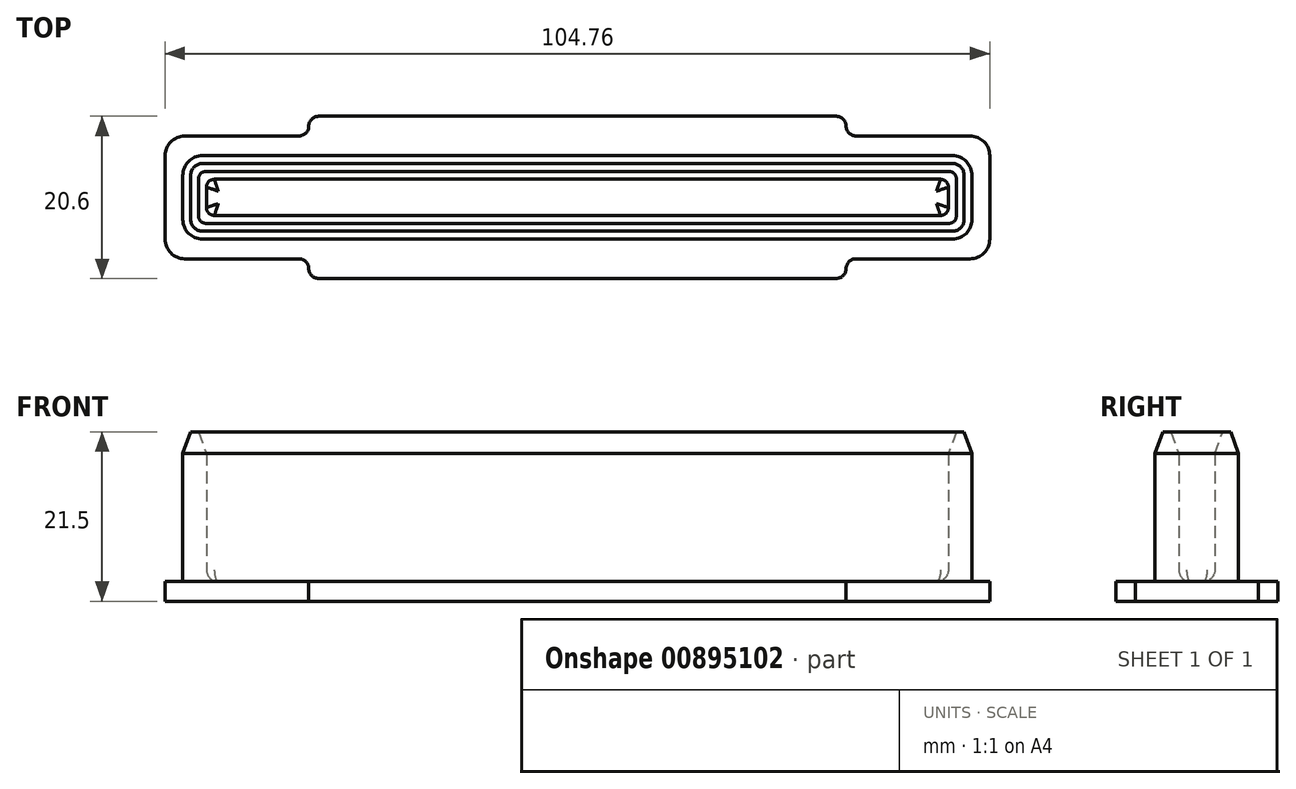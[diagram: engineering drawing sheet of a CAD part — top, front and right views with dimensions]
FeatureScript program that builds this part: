
annotation { "Feature Type Name" : "Feature", "Feature Type Description" : "" }
export const myFeature = defineFeature(function(context is Context, id is Id, definition is map)
    precondition{}
    {
        {
            var Q0;
            Q0=qCreatedBy(makeId("Top.planeOp"),FACE);
            var sketch = newSketch(context, id + "F0", { "sketchPlane" : qUnion([Q0])});
            skLineSegment(sketch, "E0.bottom", {"start": v(50.12, 5.3) * mm, "end": v(-50.12, 5.3) * mm});
            skLineSegment(sketch, "E0.top", {"start": v(50.12, -5.3) * mm, "end": v(-50.12, -5.3) * mm});
            skLineSegment(sketch, "E0.left", {"start": v(50.12, 5.3) * mm, "end": v(50.12, -5.3) * mm});
            skLineSegment(sketch, "E0.right", {"start": v(-50.12, 5.3) * mm, "end": v(-50.12, -5.3) * mm});
            skPoint(sketch, "E0.middle", {"position": v(0, 0) * mm});
            skLineSegment(sketch, "E1.bottom", {"start": v(52.38, 7.8) * mm, "end": v(-52.38, 7.8) * mm});
            skLineSegment(sketch, "E1.top", {"start": v(52.38, -7.8) * mm, "end": v(-52.38, -7.8) * mm});
            skLineSegment(sketch, "E1.left", {"start": v(52.38, 7.8) * mm, "end": v(52.38, -7.8) * mm});
            skLineSegment(sketch, "E1.right", {"start": v(-52.38, 7.8) * mm, "end": v(-52.38, -7.8) * mm});
            skLineSegment(sketch, "E2", {"start": v(0, -22.04) * mm, "end": v(0, 22.45) * mm, "construction": true});
            skLineSegment(sketch, "E3", {"start": v(0, 10.3) * mm, "end": v(34.12, 10.3) * mm});
            skLineSegment(sketch, "E4", {"start": v(34.12, 10.3) * mm, "end": v(34.12, 7.8) * mm});
            skLineSegment(sketch, "E5.MirrorCS", {"start": v(0, 10.3) * mm, "end": v(-34.12, 10.3) * mm});
            skLineSegment(sketch, "E6.MirrorCS", {"start": v(-34.12, 10.3) * mm, "end": v(-34.12, 7.8) * mm});
            skLineSegment(sketch, "E7.MirrorCS", {"start": v(-34.12, -10.3) * mm, "end": v(-34.12, -7.8) * mm});
            skLineSegment(sketch, "E8.MirrorCS", {"start": v(0, -10.3) * mm, "end": v(-34.12, -10.3) * mm});
            skLineSegment(sketch, "E9.MirrorCS", {"start": v(34.13, -10.3) * mm, "end": v(34.13, -7.8) * mm});
            skLineSegment(sketch, "E10.MirrorCS", {"start": v(0, -10.3) * mm, "end": v(34.12, -10.3) * mm});
            skSolve(sketch);
        }
        {
            var Q0;
            Q0=makeQuery(id+"F0.imprint","IMPRINT",FACE,{"disambiguationData":[TD([[makeQuery(id+"F0.imprint","IMPRINT",EDGE,{"derivedFrom":sQuery(id+"F0.wireOp",EDGE,"E0.bottom")}),1.0]])]});
            extrude(context, id + "F1", {"entities" : qUnion([Q0]), "depth" : 19 * mm, "offsetDistance" : 25 * mm});
        }
        {
            var Q0;
            Q0=makeQuery(id+"F1.opExtrude","CAP_FACE",FACE,{"disambiguationData":[OSD([sQuery(id+"F0.wireOp",EDGE,"E0.bottom"),sQuery(id+"F0.wireOp",EDGE,"E0.top"),sQuery(id+"F0.wireOp",EDGE,"E0.left"),sQuery(id+"F0.wireOp",EDGE,"E0.right")])],"isStart":false});
            shell(context, id + "F2", {"entities" : qUnion([Q0]), "thickness" : 3 * mm});
        }
        {
            var Q0;
            Q0=makeQuery(id+"F2.opShell","OFFSET_FACE",FACE,{"disambiguationData":[OSD([sQuery(id+"F0.wireOp",EDGE,"E0.bottom"),sQuery(id+"F0.wireOp",EDGE,"E0.top"),sQuery(id+"F0.wireOp",EDGE,"E0.left"),sQuery(id+"F0.wireOp",EDGE,"E0.right")])]});
            extrude(context, id + "F3", {"entities" : qUnion([Q0]), "operationType" : NewBodyOperationType.REMOVE, "oppositeDirection" : true, "depth" : 25 * mm, "offsetDistance" : 25 * mm});
        }
        {
            var Q0;
            Q0=makeQuery(id+"F0.imprint","IMPRINT",FACE,{"disambiguationData":[TD([[makeQuery(id+"F0.imprint","IMPRINT",EDGE,{"derivedFrom":sQuery(id+"F0.wireOp",EDGE,"E3")}),-1.0]])]});
            var Q1;
            Q1=makeQuery(id+"F0.imprint","IMPRINT",FACE,{"disambiguationData":[TD([[makeQuery(id+"F0.imprint","IMPRINT",EDGE,{"derivedFrom":sQuery(id+"F0.wireOp",EDGE,"E0.bottom")}),-1.0]])]});
            var Q2;
            {var subQ0=sQuery(id+"F0.wireOp",EDGE,"E7.MirrorCS");Q2=makeQuery(id+"F0.imprint","IMPRINT",FACE,{"disambiguationData":[TD([[makeQuery(id+"F0.imprint","IMPRINT",EDGE,{"derivedFrom":subQ0}),-1.0]])]});}
            var Q3;
            Q3=makeQuery(id+"F0.imprint","IMPRINT",FACE,{"disambiguationData":[TD([[makeQuery(id+"F0.imprint","IMPRINT",EDGE,{"derivedFrom":sQuery(id+"F0.wireOp",EDGE,"E0.bottom")}),1.0]])]});
            extrude(context, id + "F4", {"entities" : qUnion([Q0, Q1, Q2, Q3]), "operationType" : NewBodyOperationType.ADD, "oppositeDirection" : true, "depth" : 2.5 * mm, "offsetDistance" : 25 * mm});
        }
        {
            var Q0;
            Q0=makeQuery(id+"F4.opExtrude","SWEPT_EDGE",EDGE,{"disambiguationData":[OSD([sQuery(id+"F0.wireOp",EDGE,"E1.top"),sQuery(id+"F0.wireOp",EDGE,"E1.right")])]});
            var Q1;
            Q1=makeQuery(id+"F4.opExtrude","SWEPT_EDGE",EDGE,{"disambiguationData":[OSD([sQuery(id+"F0.wireOp",EDGE,"E1.bottom"),sQuery(id+"F0.wireOp",EDGE,"E1.right")])]});
            var Q2;
            Q2=makeQuery(id+"F4.opExtrude","SWEPT_EDGE",EDGE,{"disambiguationData":[OSD([sQuery(id+"F0.wireOp",EDGE,"E1.bottom"),sQuery(id+"F0.wireOp",EDGE,"E1.left")])]});
            var Q3;
            Q3=makeQuery(id+"F1.opExtrude","SWEPT_EDGE",EDGE,{"disambiguationData":[OSD([sQuery(id+"F0.wireOp",EDGE,"E0.bottom"),sQuery(id+"F0.wireOp",EDGE,"E0.left")])]});
            var Q4;
            Q4=makeQuery(id+"F1.opExtrude","SWEPT_EDGE",EDGE,{"disambiguationData":[OSD([sQuery(id+"F0.wireOp",EDGE,"E0.top"),sQuery(id+"F0.wireOp",EDGE,"E0.left")])]});
            var Q5;
            Q5=makeQuery(id+"F1.opExtrude","SWEPT_EDGE",EDGE,{"disambiguationData":[OSD([sQuery(id+"F0.wireOp",EDGE,"E0.top"),sQuery(id+"F0.wireOp",EDGE,"E0.right")])]});
            var Q6;
            Q6=makeQuery(id+"F1.opExtrude","SWEPT_EDGE",EDGE,{"disambiguationData":[OSD([sQuery(id+"F0.wireOp",EDGE,"E0.bottom"),sQuery(id+"F0.wireOp",EDGE,"E0.right")])]});
            var Q7;
            Q7=makeQuery(id+"F4.opExtrude","SWEPT_EDGE",EDGE,{"disambiguationData":[OSD([sQuery(id+"F0.wireOp",EDGE,"E1.top"),sQuery(id+"F0.wireOp",EDGE,"E1.left")])]});
            fillet(context, id + "F5", {"entities" : qUnion([Q0, Q1, Q2, Q3, Q4, Q5, Q6, Q7]), "radius" : 2.5 * mm, "tangentPropagation" : true, "allowEdgeOverflow" : false});
        }
        {
            var Q0;
            {var subQ0=sQuery(id+"F0.wireOp",EDGE,"E0.top");Q0=makeQuery(id+"F2.opShell","OFFSET_EDGE",EDGE,{"disambiguationData":[OSD([subQ0]),TDD([makeQuery(id+"F1.opExtrude","CAP_EDGE",EDGE,{"disambiguationData":[OSD([subQ0])],"isStart":false})])]});}
            var Q1;
            Q1=makeQuery(id+"F1.opExtrude","CAP_EDGE",EDGE,{"disambiguationData":[OSD([sQuery(id+"F0.wireOp",EDGE,"E0.top")])],"isStart":false});
            var Q2;
            Q2=makeQuery(id+"F1.opExtrude","CAP_EDGE",EDGE,{"disambiguationData":[OSD([sQuery(id+"F0.wireOp",EDGE,"E0.right")])],"isStart":false});
            var Q3;
            Q3=makeQuery(id+"F1.opExtrude","CAP_EDGE",EDGE,{"disambiguationData":[OSD([sQuery(id+"F0.wireOp",EDGE,"E0.bottom")])],"isStart":false});
            var Q4;
            Q4=makeQuery(id+"F1.opExtrude","CAP_EDGE",EDGE,{"disambiguationData":[OSD([sQuery(id+"F0.wireOp",EDGE,"E0.left")])],"isStart":false});
            var Q5;
            {var subQ0=sQuery(id+"F0.wireOp",EDGE,"E0.left");Q5=makeQuery(id+"F2.opShell","OFFSET_EDGE",EDGE,{"disambiguationData":[OSD([subQ0]),TDD([makeQuery(id+"F1.opExtrude","CAP_EDGE",EDGE,{"disambiguationData":[OSD([subQ0])],"isStart":false})])]});}
            var Q6;
            {var subQ0=sQuery(id+"F0.wireOp",EDGE,"E0.bottom");Q6=makeQuery(id+"F2.opShell","OFFSET_EDGE",EDGE,{"disambiguationData":[OSD([subQ0]),TDD([makeQuery(id+"F1.opExtrude","CAP_EDGE",EDGE,{"disambiguationData":[OSD([subQ0])],"isStart":false})])]});}
            var Q7;
            {var subQ0=sQuery(id+"F0.wireOp",EDGE,"E0.right");Q7=makeQuery(id+"F2.opShell","OFFSET_EDGE",EDGE,{"disambiguationData":[OSD([subQ0]),TDD([makeQuery(id+"F1.opExtrude","CAP_EDGE",EDGE,{"disambiguationData":[OSD([subQ0])],"isStart":false})])]});}
            chamfer(context, id + "F6", {"entities" : qUnion([Q0, Q1, Q2, Q3, Q4, Q5, Q6, Q7]), "chamferType" : ChamferType.OFFSET_ANGLE, "width" : 1 * mm, "oppositeDirection" : false, "angle" : 70 * degree, "tangentPropagation" : true});
        }
        {
            var Q0;
            Q0=makeQuery(id+"F1.opExtrude","CAP_EDGE",EDGE,{"disambiguationData":[OSD([sQuery(id+"F0.wireOp",EDGE,"E0.bottom")])],"isStart":true});
            var Q1;
            Q1=makeQuery(id+"F1.opExtrude","CAP_EDGE",EDGE,{"disambiguationData":[OSD([sQuery(id+"F0.wireOp",EDGE,"E0.left")])],"isStart":true});
            var Q2;
            Q2=makeQuery(id+"F1.opExtrude","CAP_EDGE",EDGE,{"disambiguationData":[OSD([sQuery(id+"F0.wireOp",EDGE,"E0.top")])],"isStart":true});
            var Q3;
            Q3=makeQuery(id+"F1.opExtrude","CAP_EDGE",EDGE,{"disambiguationData":[OSD([sQuery(id+"F0.wireOp",EDGE,"E0.right")])],"isStart":true});
            var Q4;
            {var subQ0=sQuery(id+"F0.wireOp",EDGE,"E0.right");var subQ1=sQuery(id+"F0.wireOp",EDGE,"E0.bottom");Q4=makeQuery(id+"F3.boolean.opBoolean","MERGE",EDGE,{"derivedFrom":[makeQuery(id+"F2.opShell","OFFSET_EDGE",EDGE,{"disambiguationData":[OSD([subQ1,subQ0])]})],"fromTools":[makeQuery(id+"F3.opExtrude","SWEPT_EDGE",EDGE,{"disambiguationData":[OSD([subQ1,subQ0])]})]});}
            var Q5;
            {var subQ0=sQuery(id+"F0.wireOp",EDGE,"E0.left");var subQ1=sQuery(id+"F0.wireOp",EDGE,"E0.bottom");Q5=makeQuery(id+"F3.boolean.opBoolean","MERGE",EDGE,{"derivedFrom":[makeQuery(id+"F2.opShell","OFFSET_EDGE",EDGE,{"disambiguationData":[OSD([subQ1,subQ0])]})],"fromTools":[makeQuery(id+"F3.opExtrude","SWEPT_EDGE",EDGE,{"disambiguationData":[OSD([subQ1,subQ0])]})]});}
            var Q6;
            {var subQ0=sQuery(id+"F0.wireOp",EDGE,"E0.right");var subQ1=sQuery(id+"F0.wireOp",EDGE,"E0.top");Q6=makeQuery(id+"F3.boolean.opBoolean","MERGE",EDGE,{"derivedFrom":[makeQuery(id+"F2.opShell","OFFSET_EDGE",EDGE,{"disambiguationData":[OSD([subQ1,subQ0])]})],"fromTools":[makeQuery(id+"F3.opExtrude","SWEPT_EDGE",EDGE,{"disambiguationData":[OSD([subQ1,subQ0])]})]});}
            var Q7;
            {var subQ0=sQuery(id+"F0.wireOp",EDGE,"E0.left");var subQ1=sQuery(id+"F0.wireOp",EDGE,"E0.top");Q7=makeQuery(id+"F3.boolean.opBoolean","MERGE",EDGE,{"derivedFrom":[makeQuery(id+"F2.opShell","OFFSET_EDGE",EDGE,{"disambiguationData":[OSD([subQ1,subQ0])]})],"fromTools":[makeQuery(id+"F3.opExtrude","SWEPT_EDGE",EDGE,{"disambiguationData":[OSD([subQ1,subQ0])]})]});}
            var Q8;
            {var subQ0=sQuery(id+"F0.wireOp",EDGE,"E0.right");var subQ1=sQuery(id+"F0.wireOp",EDGE,"E0.bottom");Q8=makeQuery(id+"F6.opChamfer","BLEND_EDGE",EDGE,{"blendedFrom":[makeQuery(id+"F2.opShell","OFFSET_EDGE",EDGE,{"disambiguationData":[OSD([subQ1]),TDD([makeQuery(id+"F1.opExtrude","CAP_EDGE",EDGE,{"disambiguationData":[OSD([subQ1])],"isStart":false})])]}),makeQuery(id+"F2.opShell","OFFSET_EDGE",EDGE,{"disambiguationData":[OSD([subQ0]),TDD([makeQuery(id+"F1.opExtrude","CAP_EDGE",EDGE,{"disambiguationData":[OSD([subQ0])],"isStart":false})])]})],"blendedInto":[]});}
            var Q9;
            {var subQ0=sQuery(id+"F0.wireOp",EDGE,"E0.left");var subQ1=sQuery(id+"F0.wireOp",EDGE,"E0.bottom");Q9=makeQuery(id+"F6.opChamfer","BLEND_EDGE",EDGE,{"blendedFrom":[makeQuery(id+"F2.opShell","OFFSET_EDGE",EDGE,{"disambiguationData":[OSD([subQ1]),TDD([makeQuery(id+"F1.opExtrude","CAP_EDGE",EDGE,{"disambiguationData":[OSD([subQ1])],"isStart":false})])]}),makeQuery(id+"F2.opShell","OFFSET_EDGE",EDGE,{"disambiguationData":[OSD([subQ0]),TDD([makeQuery(id+"F1.opExtrude","CAP_EDGE",EDGE,{"disambiguationData":[OSD([subQ0])],"isStart":false})])]})],"blendedInto":[]});}
            var Q10;
            {var subQ0=sQuery(id+"F0.wireOp",EDGE,"E0.right");var subQ1=sQuery(id+"F0.wireOp",EDGE,"E0.top");Q10=makeQuery(id+"F6.opChamfer","BLEND_EDGE",EDGE,{"blendedFrom":[makeQuery(id+"F2.opShell","OFFSET_EDGE",EDGE,{"disambiguationData":[OSD([subQ1]),TDD([makeQuery(id+"F1.opExtrude","CAP_EDGE",EDGE,{"disambiguationData":[OSD([subQ1])],"isStart":false})])]}),makeQuery(id+"F2.opShell","OFFSET_EDGE",EDGE,{"disambiguationData":[OSD([subQ0]),TDD([makeQuery(id+"F1.opExtrude","CAP_EDGE",EDGE,{"disambiguationData":[OSD([subQ0])],"isStart":false})])]})],"blendedInto":[]});}
            var Q11;
            {var subQ0=sQuery(id+"F0.wireOp",EDGE,"E0.left");var subQ1=sQuery(id+"F0.wireOp",EDGE,"E0.top");Q11=makeQuery(id+"F6.opChamfer","BLEND_EDGE",EDGE,{"blendedFrom":[makeQuery(id+"F2.opShell","OFFSET_EDGE",EDGE,{"disambiguationData":[OSD([subQ1]),TDD([makeQuery(id+"F1.opExtrude","CAP_EDGE",EDGE,{"disambiguationData":[OSD([subQ1])],"isStart":false})])]}),makeQuery(id+"F2.opShell","OFFSET_EDGE",EDGE,{"disambiguationData":[OSD([subQ0]),TDD([makeQuery(id+"F1.opExtrude","CAP_EDGE",EDGE,{"disambiguationData":[OSD([subQ0])],"isStart":false})])]})],"blendedInto":[]});}
            fillet(context, id + "F7", {"entities" : qUnion([Q0, Q1, Q2, Q3, Q4, Q5, Q6, Q7, Q8, Q9, Q10, Q11]), "radius" : 1 * mm, "tangentPropagation" : true, "allowEdgeOverflow" : false});
        }
        {
            var Q0;
            Q0=makeQuery(id+"F4.opExtrude","SWEPT_EDGE",EDGE,{"disambiguationData":[OSD([sQuery(id+"F0.wireOp",EDGE,"E5.MirrorCS"),sQuery(id+"F0.wireOp",EDGE,"E6.MirrorCS")])]});
            var Q1;
            Q1=makeQuery(id+"F4.opExtrude","SWEPT_EDGE",EDGE,{"disambiguationData":[OSD([sQuery(id+"F0.wireOp",EDGE,"E3"),sQuery(id+"F0.wireOp",EDGE,"E4")])]});
            var Q2;
            Q2=makeQuery(id+"F4.opExtrude","SWEPT_EDGE",EDGE,{"disambiguationData":[OSD([sQuery(id+"F0.wireOp",EDGE,"E9.MirrorCS"),sQuery(id+"F0.wireOp",EDGE,"E10.MirrorCS")])]});
            var Q3;
            Q3=makeQuery(id+"F4.opExtrude","SWEPT_EDGE",EDGE,{"disambiguationData":[OSD([sQuery(id+"F0.wireOp",EDGE,"E7.MirrorCS"),sQuery(id+"F0.wireOp",EDGE,"E8.MirrorCS")])]});
            var Q4;
            Q4=makeQuery(id+"F4.opExtrude","SWEPT_EDGE",EDGE,{"disambiguationData":[OSD([sQuery(id+"F0.wireOp",EDGE,"E1.top"),sQuery(id+"F0.wireOp",EDGE,"E7.MirrorCS")])]});
            var Q5;
            Q5=makeQuery(id+"F4.opExtrude","SWEPT_EDGE",EDGE,{"disambiguationData":[OSD([sQuery(id+"F0.wireOp",EDGE,"E1.bottom"),sQuery(id+"F0.wireOp",EDGE,"E6.MirrorCS")])]});
            var Q6;
            Q6=makeQuery(id+"F4.opExtrude","SWEPT_EDGE",EDGE,{"disambiguationData":[OSD([sQuery(id+"F0.wireOp",EDGE,"E1.bottom"),sQuery(id+"F0.wireOp",EDGE,"E4")])]});
            var Q7;
            Q7=makeQuery(id+"F4.opExtrude","SWEPT_EDGE",EDGE,{"disambiguationData":[OSD([sQuery(id+"F0.wireOp",EDGE,"E1.top"),sQuery(id+"F0.wireOp",EDGE,"E9.MirrorCS")])]});
            fillet(context, id + "F8", {"entities" : qUnion([Q0, Q1, Q2, Q3, Q4, Q5, Q6, Q7]), "radius" : 1.25 * mm, "tangentPropagation" : true, "allowEdgeOverflow" : false});
        }
        {
            var Q0;
            {var subQ0=sQuery(id+"F0.wireOp",EDGE,"E0.right");Q0=makeQuery(id+"F3.boolean.opBoolean","INTERSECT",EDGE,{"derivedFrom":[makeQuery(id+"F1.opExtrude","CAP_FACE",FACE,{"disambiguationData":[OSD([sQuery(id+"F0.wireOp",EDGE,"E0.bottom"),sQuery(id+"F0.wireOp",EDGE,"E0.top"),sQuery(id+"F0.wireOp",EDGE,"E0.left"),subQ0])],"isStart":true}),makeQuery(id+"F3.opExtrude","SWEPT_FACE",FACE,{"disambiguationData":[OSD([subQ0])]})]});}
            var Q1;
            {var subQ0=sQuery(id+"F0.wireOp",EDGE,"E0.bottom");Q1=makeQuery(id+"F3.boolean.opBoolean","INTERSECT",EDGE,{"derivedFrom":[makeQuery(id+"F1.opExtrude","CAP_FACE",FACE,{"disambiguationData":[OSD([subQ0,sQuery(id+"F0.wireOp",EDGE,"E0.top"),sQuery(id+"F0.wireOp",EDGE,"E0.left"),sQuery(id+"F0.wireOp",EDGE,"E0.right")])],"isStart":true}),makeQuery(id+"F3.opExtrude","SWEPT_FACE",FACE,{"disambiguationData":[OSD([subQ0])]})]});}
            var Q2;
            {var subQ0=sQuery(id+"F0.wireOp",EDGE,"E0.top");Q2=makeQuery(id+"F3.boolean.opBoolean","INTERSECT",EDGE,{"derivedFrom":[makeQuery(id+"F1.opExtrude","CAP_FACE",FACE,{"disambiguationData":[OSD([sQuery(id+"F0.wireOp",EDGE,"E0.bottom"),subQ0,sQuery(id+"F0.wireOp",EDGE,"E0.left"),sQuery(id+"F0.wireOp",EDGE,"E0.right")])],"isStart":true}),makeQuery(id+"F3.opExtrude","SWEPT_FACE",FACE,{"disambiguationData":[OSD([subQ0])]})]});}
            var Q3;
            {var subQ0=sQuery(id+"F0.wireOp",EDGE,"E0.left");Q3=makeQuery(id+"F3.boolean.opBoolean","INTERSECT",EDGE,{"derivedFrom":[makeQuery(id+"F1.opExtrude","CAP_FACE",FACE,{"disambiguationData":[OSD([sQuery(id+"F0.wireOp",EDGE,"E0.bottom"),sQuery(id+"F0.wireOp",EDGE,"E0.top"),subQ0,sQuery(id+"F0.wireOp",EDGE,"E0.right")])],"isStart":true}),makeQuery(id+"F3.opExtrude","SWEPT_FACE",FACE,{"disambiguationData":[OSD([subQ0])]})]});}
            fillet(context, id + "F9", {"entities" : qUnion([Q0, Q1, Q2, Q3]), "radius" : 1.5 * mm, "tangentPropagation" : true, "allowEdgeOverflow" : false});
        }
    });
